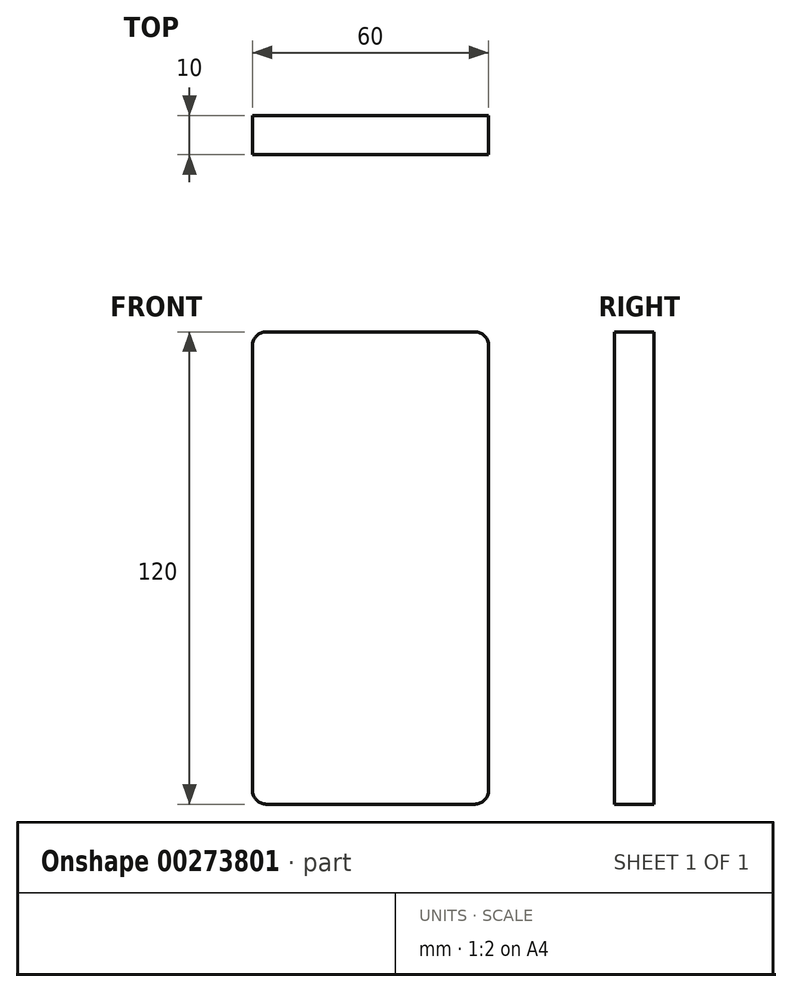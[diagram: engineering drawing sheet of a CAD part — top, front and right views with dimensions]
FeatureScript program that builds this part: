
annotation { "Feature Type Name" : "Feature", "Feature Type Description" : "" }
export const myFeature = defineFeature(function(context is Context, id is Id, definition is map)
    precondition{}
    {
        {
            var Q0;
            Q0=qCreatedBy(makeId("Front.planeOp"),FACE);
            var sketch = newSketch(context, id + "F0", { "sketchPlane" : qUnion([Q0])});
            skLineSegment(sketch, "E0.bottom", {"start": v(-26.5, 60) * mm, "end": v(26.5, 60) * mm});
            skLineSegment(sketch, "E0.top", {"start": v(-26.5, -60) * mm, "end": v(26.5, -60) * mm});
            skLineSegment(sketch, "E0.left", {"start": v(-30, 56.5) * mm, "end": v(-30, -56.5) * mm});
            skLineSegment(sketch, "E0.right", {"start": v(30, 56.5) * mm, "end": v(30, -56.5) * mm});
            skPoint(sketch, "E0.middle", {"position": v(0, 0) * mm});
            skPoint(sketch, "E1.visualSharp", {"position": v(-30, 60) * mm});
            skArc(sketch, "E1.filletArc", {"start": v(-26.5, 60) * mm, "mid": v(-28.97, 58.97) * mm, "end": v(-30, 56.5) * mm});
            skPoint(sketch, "E2.visualSharp", {"position": v(30, 60) * mm});
            skArc(sketch, "E2.filletArc", {"start": v(30, 56.5) * mm, "mid": v(28.97, 58.97) * mm, "end": v(26.5, 60) * mm});
            skPoint(sketch, "E3.visualSharp", {"position": v(30, -60) * mm});
            skArc(sketch, "E3.filletArc", {"start": v(26.5, -60) * mm, "mid": v(28.97, -58.97) * mm, "end": v(30, -56.5) * mm});
            skPoint(sketch, "E4.visualSharp", {"position": v(-30, -60) * mm});
            skArc(sketch, "E4.filletArc", {"start": v(-30, -56.5) * mm, "mid": v(-28.97, -58.97) * mm, "end": v(-26.5, -60) * mm});
            skSolve(sketch);
        }
        {
            var Q0;
            Q0=makeQuery(id+"F0.imprint","IMPRINT",FACE,{"disambiguationData":[TD([[makeQuery(id+"F0.imprint","IMPRINT",EDGE,{"derivedFrom":sQuery(id+"F0.wireOp",EDGE,"E0.bottom")}),-1.0]])]});
            extrude(context, id + "F1", {"entities" : qUnion([Q0]), "depth" : 10 * mm});
        }
    });
